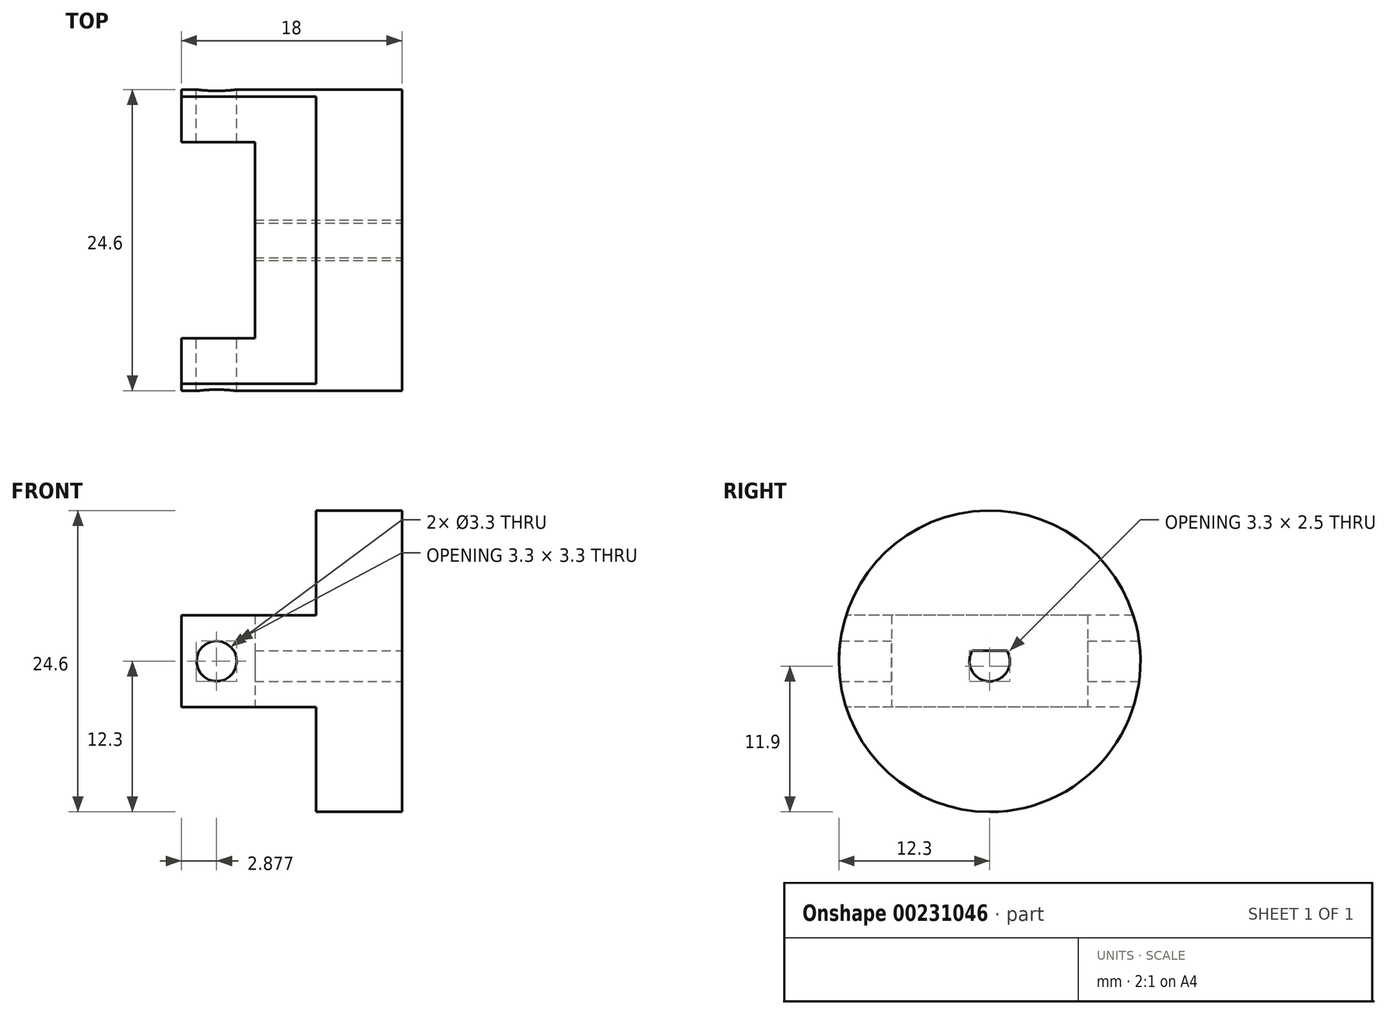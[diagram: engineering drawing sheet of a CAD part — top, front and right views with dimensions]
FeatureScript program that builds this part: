
annotation { "Feature Type Name" : "Feature", "Feature Type Description" : "" }
export const myFeature = defineFeature(function(context is Context, id is Id, definition is map)
    precondition{}
    {
        {
            var Q0;
            Q0=qCreatedBy(makeId("Top.planeOp"),FACE);
            var sketch = newSketch(context, id + "F0", { "sketchPlane" : qUnion([Q0])});
            skLineSegment(sketch, "E0.bottom", {"start": v(5.5, 12.5) * mm, "end": v(-5.5, 12.5) * mm});
            skLineSegment(sketch, "E0.top", {"start": v(5.5, -12.5) * mm, "end": v(-5.5, -12.5) * mm});
            skLineSegment(sketch, "E0.left", {"start": v(5.5, 12.5) * mm, "end": v(5.5, -12.5) * mm});
            skLineSegment(sketch, "E0.right", {"start": v(-5.5, 12.5) * mm, "end": v(-5.5, -12.5) * mm});
            skPoint(sketch, "E0.middle", {"position": v(0, 0) * mm});
            skLineSegment(sketch, "E1.bottom", {"start": v(0.5, 8) * mm, "end": v(-11.5, 8) * mm});
            skLineSegment(sketch, "E1.top", {"start": v(0.5, -8) * mm, "end": v(-11.5, -8) * mm});
            skLineSegment(sketch, "E1.left", {"start": v(0.5, 8) * mm, "end": v(0.5, -8) * mm});
            skLineSegment(sketch, "E1.right", {"start": v(-11.5, 8) * mm, "end": v(-11.5, -8) * mm});
            skPoint(sketch, "E1.middle", {"position": v(-5.5, 0) * mm});
            skSolve(sketch);
        }
        {
            var Q0;
            {var subQ1=sQuery(id+"F0.wireOp",EDGE,"E0.bottom");Q0=makeQuery(id+"F0.imprint","IMPRINT",FACE,{"disambiguationData":[TD([[makeQuery(id+"F0.imprint","IMPRINT",EDGE,{"derivedFrom":subQ1}),1.0]])]});}
            extrude(context, id + "F1", {"entities" : qUnion([Q0]), "depth" : 7.5 * mm});
        }
        {
            var Q0;
            Q0=makeQuery(id+"F1.opExtrude","SWEPT_FACE",FACE,{"disambiguationData":[OSD([sQuery(id+"F0.wireOp",EDGE,"E0.bottom")])]});
            var sketch = newSketch(context, id + "F2", { "sketchPlane" : qUnion([Q0])});
            skLineSegment(sketch, "E2", {"start": v(-0.5, 7.5) * mm, "end": v(-0.5, 0) * mm});
            skLineSegment(sketch, "E3", {"start": v(5.5, 3.75) * mm, "end": v(-0.5, 3.75) * mm});
            skCircle(sketch, "E4", {"center": v(2.62, 3.75) * mm, "radius": 1.65 * mm});
            skSolve(sketch);
        }
        {
            var Q0;
            {var subQ0=sQuery(id+"F2.wireOp",EDGE,"E4");var subQ1=sQuery(id+"F2.wireOp",EDGE,"E3");var subQ2=makeQuery(id+"F2.imprint","INTERSECT",VERTEX,{"disambiguationData":[OD(0.0)],"derivedFrom":[subQ1,subQ0]});Q0=makeQuery(id+"F2.imprint","IMPRINT",FACE,{"disambiguationData":[TD([[makeQuery(id+"F2.imprint","IMPRINT",EDGE,{"disambiguationData":[TD([[subQ2,-1.0]])],"derivedFrom":subQ1}),-1.0]])]});}
            var Q1;
            {var subQ0=sQuery(id+"F2.wireOp",EDGE,"E4");var subQ1=sQuery(id+"F2.wireOp",EDGE,"E3");var subQ2=makeQuery(id+"F2.imprint","INTERSECT",VERTEX,{"disambiguationData":[OD(0.0)],"derivedFrom":[subQ1,subQ0]});Q1=makeQuery(id+"F2.imprint","IMPRINT",FACE,{"disambiguationData":[TD([[makeQuery(id+"F2.imprint","IMPRINT",EDGE,{"disambiguationData":[TD([[subQ2,-1.0]])],"derivedFrom":subQ1}),1.0]])]});}
            extrude(context, id + "F3", {"entities" : qUnion([Q0, Q1]), "operationType" : NewBodyOperationType.REMOVE, "endBound" : BoundingType.THROUGH_ALL, "oppositeDirection" : true, "depth" : 25 * mm});
        }
        {
            var Q0;
            Q0=makeQuery(id+"F1.opExtrude","SWEPT_FACE",FACE,{"disambiguationData":[OSD([sQuery(id+"F0.wireOp",EDGE,"E0.left")])]});
            var sketch = newSketch(context, id + "F4", { "sketchPlane" : qUnion([Q0])});
            skLineSegment(sketch, "E5", {"start": v(0, 7.5) * mm, "end": v(0, 0) * mm});
            skCircle(sketch, "E6", {"center": v(0, 3.75) * mm, "radius": 12.3 * mm});
            skSolve(sketch);
        }
        {
            var Q0;
            Q0=makeQuery(id+"F4.imprint","IMPRINT",FACE,{"disambiguationData":[TD([[makeQuery(id+"F4.imprint","IMPRINT",EDGE,{"derivedFrom":sQuery(id+"F4.wireOp",EDGE,"E6")}),1.0]])]});
            var Q1;
            {var subQ0=sQuery(id+"F4.wireOp",EDGE,"E5");Q1=makeQuery(id+"F4.imprint","IMPRINT",FACE,{"disambiguationData":[TD([[makeQuery(id+"F4.imprint","IMPRINT",EDGE,{"derivedFrom":subQ0}),-1.0]])]});}
            var Q2;
            {var subQ0=sQuery(id+"F4.wireOp",EDGE,"E5");Q2=makeQuery(id+"F4.imprint","IMPRINT",FACE,{"disambiguationData":[TD([[makeQuery(id+"F4.imprint","IMPRINT",EDGE,{"derivedFrom":subQ0}),1.0]])]});}
            extrude(context, id + "F5", {"entities" : qUnion([Q0, Q1, Q2]), "operationType" : NewBodyOperationType.ADD, "depth" : 7 * mm});
        }
        {
            var Q0;
            Q0=makeQuery(id+"F5.opExtrude","CAP_FACE",FACE,{"disambiguationData":[OSD([sQuery(id+"F4.wireOp",EDGE,"E6")])],"isStart":false});
            var sketch = newSketch(context, id + "F6", { "sketchPlane" : qUnion([Q0])});
            skLineSegment(sketch, "E7", {"start": v(0, 16.05) * mm, "end": v(0, -8.55) * mm});
            skCircle(sketch, "E8", {"center": v(0, 3.75) * mm, "radius": 1.65 * mm});
            skLineSegment(sketch, "E9", {"start": v(-1.41, 4.6) * mm, "end": v(1.41, 4.6) * mm});
            skSolve(sketch);
        }
        {
            var Q0;
            {var subQ0=sQuery(id+"F6.wireOp",EDGE,"E9");var subQ1=sQuery(id+"F6.wireOp",EDGE,"E7");var subQ2=makeQuery(id+"F6.imprint","INTERSECT",VERTEX,{"derivedFrom":[subQ1,subQ0]});Q0=makeQuery(id+"F6.imprint","IMPRINT",FACE,{"disambiguationData":[TD([[makeQuery(id+"F6.imprint","IMPRINT",EDGE,{"disambiguationData":[TD([[subQ2,-1.0]])],"derivedFrom":subQ1}),-1.0]])]});}
            var Q1;
            {var subQ0=sQuery(id+"F6.wireOp",EDGE,"E9");var subQ1=sQuery(id+"F6.wireOp",EDGE,"E7");var subQ2=makeQuery(id+"F6.imprint","INTERSECT",VERTEX,{"derivedFrom":[subQ1,subQ0]});Q1=makeQuery(id+"F6.imprint","IMPRINT",FACE,{"disambiguationData":[TD([[makeQuery(id+"F6.imprint","IMPRINT",EDGE,{"disambiguationData":[TD([[subQ2,-1.0]])],"derivedFrom":subQ1}),1.0]])]});}
            extrude(context, id + "F7", {"entities" : qUnion([Q0, Q1]), "operationType" : NewBodyOperationType.REMOVE, "oppositeDirection" : true, "depth" : 25 * mm});
        }
        {
            var Q0;
            Q0=makeQuery(id+"F5.opExtrude","CAP_FACE",FACE,{"disambiguationData":[OSD([sQuery(id+"F4.wireOp",EDGE,"E6")])],"isStart":false});
            var sketch = newSketch(context, id + "F8", { "sketchPlane" : qUnion([Q0])});
            skCircle(sketch, "E10", {"center": v(0, 3.75) * mm, "radius": 12.3 * mm});
            skCircle(sketch, "E11", {"center": v(0, 3.75) * mm, "radius": 14.69 * mm});
            skSolve(sketch);
        }
        {
            var Q0;
            Q0=makeQuery(id+"F8.imprint","IMPRINT",FACE,{"disambiguationData":[TD([[makeQuery(id+"F8.imprint","IMPRINT",EDGE,{"derivedFrom":sQuery(id+"F8.wireOp",EDGE,"E10")}),-1.0]])]});
            extrude(context, id + "F9", {"entities" : qUnion([Q0]), "operationType" : NewBodyOperationType.REMOVE, "oppositeDirection" : true, "depth" : 25 * mm});
        }
    });
